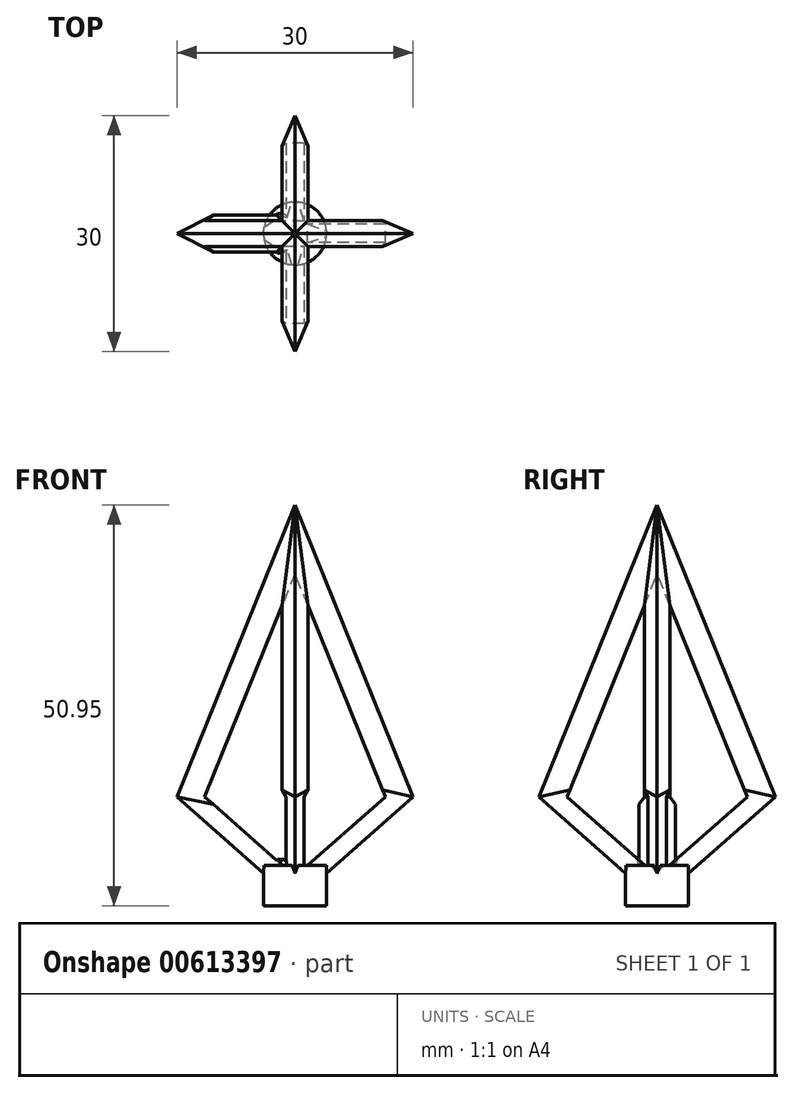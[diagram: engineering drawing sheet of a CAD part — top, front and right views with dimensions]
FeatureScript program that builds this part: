
annotation { "Feature Type Name" : "Feature", "Feature Type Description" : "" }
export const myFeature = defineFeature(function(context is Context, id is Id, definition is map)
    precondition{}
    {
        {
            var Q0;
            Q0=qCreatedBy(makeId("Front.planeOp"),FACE);
            var sketch = newSketch(context, id + "F0", { "sketchPlane" : qUnion([Q0])});
            skLineSegment(sketch, "E0", {"start": v(0, 91.96) * mm, "end": v(15, 54.88) * mm});
            skLineSegment(sketch, "E1", {"start": v(15, 54.88) * mm, "end": v(0, 41.65) * mm});
            skLineSegment(sketch, "E2", {"start": v(0, 41.65) * mm, "end": v(-15, 54.88) * mm});
            skLineSegment(sketch, "E3", {"start": v(-15, 54.88) * mm, "end": v(0, 91.96) * mm});
            skLineSegment(sketch, "E4", {"start": v(0, 41.65) * mm, "end": v(0, 91.96) * mm});
            skLineSegment(sketch, "E5", {"start": v(-15, 54.88) * mm, "end": v(15, 54.88) * mm});
            skLineSegment(sketch, "E6", {"start": v(0, 83.24) * mm, "end": v(-11.47, 54.88) * mm});
            skLineSegment(sketch, "E7", {"start": v(-11.47, 54.88) * mm, "end": v(0, 44.77) * mm});
            skLineSegment(sketch, "E8", {"start": v(0, 44.77) * mm, "end": v(11.47, 54.88) * mm});
            skLineSegment(sketch, "E9", {"start": v(11.47, 54.88) * mm, "end": v(0, 83.24) * mm});
            skSolve(sketch);
        }
        {
            var Q0;
            {var subQ0=sQuery(id+"F0.wireOp",EDGE,"E3");Q0=makeQuery(id+"F0.imprint","IMPRINT",FACE,{"disambiguationData":[TD([[makeQuery(id+"F0.imprint","IMPRINT",EDGE,{"derivedFrom":subQ0}),-1.0]])]});}
            var Q1;
            {var subQ0=sQuery(id+"F0.wireOp",EDGE,"E0");Q1=makeQuery(id+"F0.imprint","IMPRINT",FACE,{"disambiguationData":[TD([[makeQuery(id+"F0.imprint","IMPRINT",EDGE,{"derivedFrom":subQ0}),-1.0]])]});}
            var Q2;
            {var subQ0=sQuery(id+"F0.wireOp",EDGE,"E1");Q2=makeQuery(id+"F0.imprint","IMPRINT",FACE,{"disambiguationData":[TD([[makeQuery(id+"F0.imprint","IMPRINT",EDGE,{"derivedFrom":subQ0}),-1.0]])]});}
            var Q3;
            {var subQ0=sQuery(id+"F0.wireOp",EDGE,"E2");Q3=makeQuery(id+"F0.imprint","IMPRINT",FACE,{"disambiguationData":[TD([[makeQuery(id+"F0.imprint","IMPRINT",EDGE,{"derivedFrom":subQ0}),-1.0]])]});}
            extrude(context, id + "F1", {"entities" : qUnion([Q0, Q1, Q2, Q3]), "endBound" : BoundingType.SYMMETRIC, "depth" : 5 * mm, "offsetDistance" : 25 * mm});
        }
        {
            var Q0;
            Q0=qCreatedBy(makeId("Right.planeOp"),FACE);
            var sketch = newSketch(context, id + "F2", { "sketchPlane" : qUnion([Q0])});
            skLineSegment(sketch, "E10", {"start": v(0, 91.96) * mm, "end": v(15, 54.88) * mm});
            skLineSegment(sketch, "E11", {"start": v(15, 54.88) * mm, "end": v(0, 41.65) * mm});
            skLineSegment(sketch, "E12", {"start": v(0, 41.65) * mm, "end": v(-15, 54.88) * mm});
            skLineSegment(sketch, "E13", {"start": v(-15, 54.88) * mm, "end": v(0, 91.96) * mm});
            skLineSegment(sketch, "E14", {"start": v(0, 41.65) * mm, "end": v(0, 91.96) * mm});
            skLineSegment(sketch, "E15", {"start": v(-15, 54.88) * mm, "end": v(15, 54.88) * mm});
            skLineSegment(sketch, "E16", {"start": v(0, 83.24) * mm, "end": v(-11.47, 54.88) * mm});
            skLineSegment(sketch, "E17", {"start": v(-11.47, 54.88) * mm, "end": v(0, 44.77) * mm});
            skLineSegment(sketch, "E18", {"start": v(0, 44.77) * mm, "end": v(11.47, 54.88) * mm});
            skLineSegment(sketch, "E19", {"start": v(11.47, 54.88) * mm, "end": v(0, 83.24) * mm});
            skSolve(sketch);
        }
        {
            var Q0;
            {var subQ0=sQuery(id+"F2.wireOp",EDGE,"E13");Q0=makeQuery(id+"F2.imprint","IMPRINT",FACE,{"disambiguationData":[TD([[makeQuery(id+"F2.imprint","IMPRINT",EDGE,{"derivedFrom":subQ0}),-1.0]])]});}
            var Q1;
            {var subQ0=sQuery(id+"F2.wireOp",EDGE,"E12");Q1=makeQuery(id+"F2.imprint","IMPRINT",FACE,{"disambiguationData":[TD([[makeQuery(id+"F2.imprint","IMPRINT",EDGE,{"derivedFrom":subQ0}),-1.0]])]});}
            var Q2;
            {var subQ0=sQuery(id+"F2.wireOp",EDGE,"E10");Q2=makeQuery(id+"F2.imprint","IMPRINT",FACE,{"disambiguationData":[TD([[makeQuery(id+"F2.imprint","IMPRINT",EDGE,{"derivedFrom":subQ0}),-1.0]])]});}
            var Q3;
            {var subQ0=sQuery(id+"F2.wireOp",EDGE,"E11");Q3=makeQuery(id+"F2.imprint","IMPRINT",FACE,{"disambiguationData":[TD([[makeQuery(id+"F2.imprint","IMPRINT",EDGE,{"derivedFrom":subQ0}),-1.0]])]});}
            extrude(context, id + "F3", {"entities" : qUnion([Q0, Q1, Q2, Q3]), "operationType" : NewBodyOperationType.ADD, "endBound" : BoundingType.SYMMETRIC, "depth" : 5 * mm, "offsetDistance" : 25 * mm});
        }
        {
            var Q0;
            {var subQ0=sQuery(id+"F2.wireOp",EDGE,"E12");var subQ1=sQuery(id+"F2.wireOp",EDGE,"E13");Q0=makeQuery(id+"F3.boolean.opBoolean","SPLIT",EDGE,{"disambiguationData":[TD([makeQuery(id+"F3.opExtrude","SWEPT_FACE",FACE,{"disambiguationData":[OSD([subQ0])]})])],"derivedFrom":makeQuery(id+"F3.opExtrude","CAP_EDGE",EDGE,{"disambiguationData":[OSD([subQ1])],"isStart":false})});}
            chamfer(context, id + "F4", {"entities" : qUnion([Q0]), "chamferType" : ChamferType.TWO_OFFSETS, "width1" : 2.5 * mm, "oppositeDirection" : false, "width2" : 5 * mm, "tangentPropagation" : true});
        }
        {
            var Q0;
            {var subQ0=sQuery(id+"F2.wireOp",EDGE,"E12");var subQ1=sQuery(id+"F2.wireOp",EDGE,"E13");Q0=makeQuery(id+"F3.boolean.opBoolean","SPLIT",EDGE,{"disambiguationData":[TD([makeQuery(id+"F3.opExtrude","SWEPT_FACE",FACE,{"disambiguationData":[OSD([subQ0])]})])],"derivedFrom":makeQuery(id+"F3.opExtrude","CAP_EDGE",EDGE,{"disambiguationData":[OSD([subQ1])],"isStart":true})});}
            chamfer(context, id + "F5", {"entities" : qUnion([Q0]), "chamferType" : ChamferType.TWO_OFFSETS, "width1" : 5 * mm, "oppositeDirection" : false, "width2" : 2.5 * mm, "tangentPropagation" : true});
        }
        {
            var Q0;
            {var subQ0=sQuery(id+"F2.wireOp",EDGE,"E13");var subQ1=sQuery(id+"F2.wireOp",EDGE,"E12");Q0=makeQuery(id+"F3.boolean.opBoolean","SPLIT",EDGE,{"disambiguationData":[TD([makeQuery(id+"F3.opExtrude","SWEPT_FACE",FACE,{"disambiguationData":[OSD([subQ0])]})])],"derivedFrom":makeQuery(id+"F3.opExtrude","CAP_EDGE",EDGE,{"disambiguationData":[OSD([subQ1])],"isStart":false})});}
            chamfer(context, id + "F6", {"entities" : qUnion([Q0]), "chamferType" : ChamferType.TWO_OFFSETS, "width1" : 2.5 * mm, "oppositeDirection" : false, "width2" : 5 * mm, "tangentPropagation" : true});
        }
        {
            var Q0;
            {var subQ0=sQuery(id+"F2.wireOp",EDGE,"E12");var subQ1=sQuery(id+"F2.wireOp",EDGE,"E13");Q0=makeQuery(id+"F3.boolean.opBoolean","SPLIT",EDGE,{"disambiguationData":[TD([makeQuery(id+"F3.opExtrude","SWEPT_FACE",FACE,{"disambiguationData":[OSD([subQ1])]})])],"derivedFrom":makeQuery(id+"F3.opExtrude","CAP_EDGE",EDGE,{"disambiguationData":[OSD([subQ0])],"isStart":true})});}
            chamfer(context, id + "F7", {"entities" : qUnion([Q0]), "chamferType" : ChamferType.TWO_OFFSETS, "width1" : 5 * mm, "oppositeDirection" : false, "width2" : 2.5 * mm, "tangentPropagation" : true});
        }
        {
            var Q0;
            {var subQ0=sQuery(id+"F2.wireOp",EDGE,"E10");var subQ1=sQuery(id+"F2.wireOp",EDGE,"E11");Q0=makeQuery(id+"F3.boolean.opBoolean","SPLIT",EDGE,{"disambiguationData":[TD([makeQuery(id+"F3.opExtrude","SWEPT_FACE",FACE,{"disambiguationData":[OSD([subQ1])]})])],"derivedFrom":makeQuery(id+"F3.opExtrude","CAP_EDGE",EDGE,{"disambiguationData":[OSD([subQ0])],"isStart":false})});}
            chamfer(context, id + "F8", {"entities" : qUnion([Q0]), "chamferType" : ChamferType.TWO_OFFSETS, "width1" : 2.5 * mm, "oppositeDirection" : false, "width2" : 5 * mm, "tangentPropagation" : true});
        }
        {
            var Q0;
            {var subQ0=sQuery(id+"F2.wireOp",EDGE,"E10");var subQ2=sQuery(id+"F2.wireOp",EDGE,"E11");Q0=makeQuery(id+"F3.boolean.opBoolean","SPLIT",EDGE,{"disambiguationData":[TD([makeQuery(id+"F3.opExtrude","SWEPT_FACE",FACE,{"disambiguationData":[OSD([subQ2])]})])],"derivedFrom":makeQuery(id+"F3.opExtrude","CAP_EDGE",EDGE,{"disambiguationData":[OSD([subQ0])],"isStart":true})});}
            chamfer(context, id + "F9", {"entities" : qUnion([Q0]), "chamferType" : ChamferType.TWO_OFFSETS, "width1" : 5 * mm, "oppositeDirection" : false, "width2" : 2.5 * mm, "tangentPropagation" : true});
        }
        {
            var Q0;
            {var subQ0=sQuery(id+"F2.wireOp",EDGE,"E11");var subQ1=sQuery(id+"F2.wireOp",EDGE,"E10");Q0=makeQuery(id+"F3.boolean.opBoolean","SPLIT",EDGE,{"disambiguationData":[TD([makeQuery(id+"F3.opExtrude","SWEPT_FACE",FACE,{"disambiguationData":[OSD([subQ1])]})])],"derivedFrom":makeQuery(id+"F3.opExtrude","CAP_EDGE",EDGE,{"disambiguationData":[OSD([subQ0])],"isStart":true})});}
            chamfer(context, id + "F10", {"entities" : qUnion([Q0]), "chamferType" : ChamferType.TWO_OFFSETS, "width1" : 5 * mm, "oppositeDirection" : false, "width2" : 2.5 * mm, "tangentPropagation" : true});
        }
        {
            var Q0;
            {var subQ0=sQuery(id+"F2.wireOp",EDGE,"E10");var subQ2=sQuery(id+"F2.wireOp",EDGE,"E11");Q0=makeQuery(id+"F3.boolean.opBoolean","SPLIT",EDGE,{"disambiguationData":[TD([makeQuery(id+"F3.opExtrude","SWEPT_FACE",FACE,{"disambiguationData":[OSD([subQ0])]})])],"derivedFrom":makeQuery(id+"F3.opExtrude","CAP_EDGE",EDGE,{"disambiguationData":[OSD([subQ2])],"isStart":false})});}
            chamfer(context, id + "F11", {"entities" : qUnion([Q0]), "chamferType" : ChamferType.TWO_OFFSETS, "width1" : 2.5 * mm, "oppositeDirection" : false, "width2" : 5 * mm, "tangentPropagation" : true});
        }
        {
            var Q0;
            {var subQ0=sQuery(id+"F0.wireOp",EDGE,"E9");var subQ1=sQuery(id+"F0.wireOp",EDGE,"E8");var subQ2=sQuery(id+"F0.wireOp",EDGE,"E7");var subQ3=sQuery(id+"F0.wireOp",EDGE,"E6");var subQ4=sQuery(id+"F0.wireOp",EDGE,"E3");var subQ5=sQuery(id+"F0.wireOp",EDGE,"E2");var subQ6=sQuery(id+"F0.wireOp",EDGE,"E1");var subQ7=sQuery(id+"F0.wireOp",EDGE,"E0");var subQ8=makeQuery(id+"F1.opExtrude","CAP_FACE",FACE,{"disambiguationData":[OSD([subQ7,subQ6,subQ5,subQ4,subQ3,subQ2,subQ1,subQ0])],"isStart":false});var subQ9=sQuery(id+"F2.wireOp",EDGE,"E19");var subQ10=sQuery(id+"F2.wireOp",EDGE,"E18");var subQ11=sQuery(id+"F2.wireOp",EDGE,"E17");var subQ12=sQuery(id+"F2.wireOp",EDGE,"E16");var subQ13=sQuery(id+"F2.wireOp",EDGE,"E13");var subQ14=sQuery(id+"F2.wireOp",EDGE,"E12");var subQ15=sQuery(id+"F2.wireOp",EDGE,"E11");var subQ16=sQuery(id+"F2.wireOp",EDGE,"E10");var subQ17=makeQuery(id+"F3.opExtrude","CAP_FACE",FACE,{"disambiguationData":[OSD([subQ16,subQ15,subQ14,subQ13,subQ12,subQ11,subQ10,subQ9])],"isStart":true});var subQ18=makeQuery(id+"F1.opExtrude","SWEPT_FACE",FACE,{"disambiguationData":[OSD([subQ4])]});var subQ19=makeQuery(id+"F1.opExtrude","SWEPT_FACE",FACE,{"disambiguationData":[OSD([subQ7])]});var subQ20=makeQuery(id+"F3.opExtrude","CAP_FACE",FACE,{"disambiguationData":[OSD([subQ16,subQ15,subQ14,subQ13,subQ12,subQ11,subQ10,subQ9])],"isStart":false});var subQ21=makeQuery(id+"F3.opExtrude","SWEPT_FACE",FACE,{"disambiguationData":[OSD([subQ13])]});var subQ22=makeQuery(id+"F1.opExtrude","SWEPT_FACE",FACE,{"disambiguationData":[OSD([subQ6])]});var subQ23=makeQuery(id+"F3.opExtrude","SWEPT_FACE",FACE,{"disambiguationData":[OSD([subQ12])]});var subQ24=makeQuery(id+"F3.opExtrude","SWEPT_FACE",FACE,{"disambiguationData":[OSD([subQ14])]});var subQ25=makeQuery(id+"F3.opExtrude","SWEPT_FACE",FACE,{"disambiguationData":[OSD([subQ11])]});var subQ26=makeQuery(id+"F1.opExtrude","SWEPT_FACE",FACE,{"disambiguationData":[OSD([subQ5])]});Q0=makeQuery(id+"F6.opChamfer","MERGE",FACE,{"derivedFrom":[makeQuery(id+"F3.boolean.opBoolean","SPLIT",FACE,{"disambiguationData":[TD([subQ8,subQ22,subQ26,subQ17,subQ20,subQ24])],"derivedFrom":subQ8}),makeQuery(id+"F5.opChamfer","MERGE",FACE,{"derivedFrom":[makeQuery(id+"F3.boolean.opBoolean","SPLIT",FACE,{"disambiguationData":[TD([subQ8,subQ26,subQ18,makeQuery(id+"F1.opExtrude","SWEPT_FACE",FACE,{"disambiguationData":[OSD([subQ3])]}),makeQuery(id+"F1.opExtrude","SWEPT_FACE",FACE,{"disambiguationData":[OSD([subQ2])]}),subQ17,subQ24,subQ21,subQ23,subQ25])],"derivedFrom":subQ8}),makeQuery(id+"F4.opChamfer","MERGE",FACE,{"derivedFrom":[makeQuery(id+"F3.boolean.opBoolean","SPLIT",FACE,{"disambiguationData":[TD([subQ19,subQ8,subQ22,makeQuery(id+"F1.opExtrude","SWEPT_FACE",FACE,{"disambiguationData":[OSD([subQ1])]}),makeQuery(id+"F1.opExtrude","SWEPT_FACE",FACE,{"disambiguationData":[OSD([subQ0])]}),subQ20,subQ24,subQ21,subQ23,subQ25])],"derivedFrom":subQ8}),makeQuery(id+"F3.boolean.opBoolean","SPLIT",FACE,{"disambiguationData":[TD([subQ19,subQ8,subQ18,subQ17,subQ20,subQ21])],"derivedFrom":subQ8})]})]})]});}
            var sketch = newSketch(context, id + "F12", { "sketchPlane" : qUnion([Q0])});
            skLineSegment(sketch, "E20", {"start": v(-2.5, 85.78) * mm, "end": v(0, 91.96) * mm});
            skLineSegment(sketch, "E21", {"start": v(0, 91.96) * mm, "end": v(2.5, 85.78) * mm});
            skLineSegment(sketch, "E22", {"start": v(2.5, 85.78) * mm, "end": v(2.5, 91.96) * mm});
            skLineSegment(sketch, "E23", {"start": v(2.5, 91.96) * mm, "end": v(-2.5, 91.96) * mm});
            skLineSegment(sketch, "E24", {"start": v(-2.5, 91.96) * mm, "end": v(-2.5, 85.78) * mm});
            skSolve(sketch);
        }
        {
            var Q0;
            {var subQ0=sQuery(id+"F12.wireOp",EDGE,"E20");Q0=makeQuery(id+"F12.imprint","IMPRINT",FACE,{"disambiguationData":[TD([[makeQuery(id+"F12.imprint","IMPRINT",EDGE,{"derivedFrom":subQ0}),1.0]])]});}
            var Q1;
            {var subQ0=sQuery(id+"F12.wireOp",EDGE,"E21");Q1=makeQuery(id+"F12.imprint","IMPRINT",FACE,{"disambiguationData":[TD([[makeQuery(id+"F12.imprint","IMPRINT",EDGE,{"derivedFrom":subQ0}),1.0]])]});}
            extrude(context, id + "F13", {"entities" : qUnion([Q0, Q1]), "operationType" : NewBodyOperationType.REMOVE, "oppositeDirection" : true, "depth" : 25 * mm, "offsetDistance" : 25 * mm});
        }
        {
            var Q0;
            {var subQ0=sQuery(id+"F0.wireOp",EDGE,"E3");var subQ4=sQuery(id+"F0.wireOp",EDGE,"E2");var subQ5=sQuery(id+"F0.wireOp",EDGE,"E0");var subQ8=makeQuery(id+"F1.opExtrude","CAP_EDGE",EDGE,{"disambiguationData":[OSD([subQ0])],"isStart":true});Q0=makeQuery(id+"F13.boolean.opBoolean","MERGE",EDGE,{"derivedFrom":[makeQuery(id+"F3.boolean.opBoolean","SPLIT",EDGE,{"disambiguationData":[TD([makeQuery(id+"F1.opExtrude","SWEPT_FACE",FACE,{"disambiguationData":[OSD([subQ5])]})])],"derivedFrom":subQ8}),makeQuery(id+"F3.boolean.opBoolean","SPLIT",EDGE,{"disambiguationData":[TD([makeQuery(id+"F1.opExtrude","SWEPT_FACE",FACE,{"disambiguationData":[OSD([subQ4])]})])],"derivedFrom":subQ8})]});}
            chamfer(context, id + "F14", {"entities" : qUnion([Q0]), "chamferType" : ChamferType.TWO_OFFSETS, "width1" : 5 * mm, "oppositeDirection" : false, "width2" : 2.5 * mm, "tangentPropagation" : true});
        }
        {
            var Q0;
            {var subQ2=sQuery(id+"F0.wireOp",EDGE,"E3");var subQ4=sQuery(id+"F0.wireOp",EDGE,"E2");var subQ5=sQuery(id+"F0.wireOp",EDGE,"E0");var subQ8=makeQuery(id+"F1.opExtrude","CAP_EDGE",EDGE,{"disambiguationData":[OSD([subQ2])],"isStart":false});Q0=makeQuery(id+"F13.boolean.opBoolean","MERGE",EDGE,{"derivedFrom":[makeQuery(id+"F3.boolean.opBoolean","SPLIT",EDGE,{"disambiguationData":[TD([makeQuery(id+"F1.opExtrude","SWEPT_FACE",FACE,{"disambiguationData":[OSD([subQ5])]})])],"derivedFrom":subQ8}),makeQuery(id+"F3.boolean.opBoolean","SPLIT",EDGE,{"disambiguationData":[TD([makeQuery(id+"F1.opExtrude","SWEPT_FACE",FACE,{"disambiguationData":[OSD([subQ4])]})])],"derivedFrom":subQ8})]});}
            chamfer(context, id + "F15", {"entities" : qUnion([Q0]), "chamferType" : ChamferType.TWO_OFFSETS, "width1" : 2.5 * mm, "oppositeDirection" : false, "width2" : 5 * mm, "tangentPropagation" : true});
        }
        {
            var Q0;
            {var subQ2=sQuery(id+"F0.wireOp",EDGE,"E1");var subQ3=sQuery(id+"F0.wireOp",EDGE,"E3");var subQ4=sQuery(id+"F0.wireOp",EDGE,"E0");var subQ8=makeQuery(id+"F1.opExtrude","CAP_EDGE",EDGE,{"disambiguationData":[OSD([subQ4])],"isStart":false});Q0=makeQuery(id+"F13.boolean.opBoolean","MERGE",EDGE,{"derivedFrom":[makeQuery(id+"F3.boolean.opBoolean","SPLIT",EDGE,{"disambiguationData":[TD([makeQuery(id+"F1.opExtrude","SWEPT_FACE",FACE,{"disambiguationData":[OSD([subQ3])]})])],"derivedFrom":subQ8}),makeQuery(id+"F3.boolean.opBoolean","SPLIT",EDGE,{"disambiguationData":[TD([makeQuery(id+"F1.opExtrude","SWEPT_FACE",FACE,{"disambiguationData":[OSD([subQ2])]})])],"derivedFrom":subQ8})]});}
            chamfer(context, id + "F16", {"entities" : qUnion([Q0]), "chamferType" : ChamferType.TWO_OFFSETS, "width1" : 2.5 * mm, "oppositeDirection" : false, "width2" : 5 * mm, "tangentPropagation" : true});
        }
        {
            var Q0;
            {var subQ2=sQuery(id+"F0.wireOp",EDGE,"E1");var subQ3=sQuery(id+"F0.wireOp",EDGE,"E3");var subQ4=sQuery(id+"F0.wireOp",EDGE,"E0");var subQ8=makeQuery(id+"F1.opExtrude","CAP_EDGE",EDGE,{"disambiguationData":[OSD([subQ4])],"isStart":true});Q0=makeQuery(id+"F13.boolean.opBoolean","MERGE",EDGE,{"derivedFrom":[makeQuery(id+"F3.boolean.opBoolean","SPLIT",EDGE,{"disambiguationData":[TD([makeQuery(id+"F1.opExtrude","SWEPT_FACE",FACE,{"disambiguationData":[OSD([subQ3])]})])],"derivedFrom":subQ8}),makeQuery(id+"F3.boolean.opBoolean","SPLIT",EDGE,{"disambiguationData":[TD([makeQuery(id+"F1.opExtrude","SWEPT_FACE",FACE,{"disambiguationData":[OSD([subQ2])]})])],"derivedFrom":subQ8})]});}
            chamfer(context, id + "F17", {"entities" : qUnion([Q0]), "chamferType" : ChamferType.TWO_OFFSETS, "width1" : 5 * mm, "oppositeDirection" : false, "width2" : 2.5 * mm, "tangentPropagation" : true});
        }
        {
            var Q0;
            {var subQ0=sQuery(id+"F0.wireOp",EDGE,"E9");var subQ1=sQuery(id+"F0.wireOp",EDGE,"E8");var subQ2=sQuery(id+"F0.wireOp",EDGE,"E7");var subQ3=sQuery(id+"F0.wireOp",EDGE,"E6");var subQ4=sQuery(id+"F0.wireOp",EDGE,"E3");var subQ5=sQuery(id+"F0.wireOp",EDGE,"E2");var subQ6=sQuery(id+"F0.wireOp",EDGE,"E1");var subQ7=sQuery(id+"F0.wireOp",EDGE,"E0");var subQ8=makeQuery(id+"F1.opExtrude","CAP_FACE",FACE,{"disambiguationData":[OSD([subQ7,subQ6,subQ5,subQ4,subQ3,subQ2,subQ1,subQ0])],"isStart":false});var subQ9=sQuery(id+"F2.wireOp",EDGE,"E19");var subQ10=sQuery(id+"F2.wireOp",EDGE,"E18");var subQ11=sQuery(id+"F2.wireOp",EDGE,"E17");var subQ12=sQuery(id+"F2.wireOp",EDGE,"E16");var subQ13=sQuery(id+"F2.wireOp",EDGE,"E13");var subQ14=sQuery(id+"F2.wireOp",EDGE,"E12");var subQ15=sQuery(id+"F2.wireOp",EDGE,"E11");var subQ16=sQuery(id+"F2.wireOp",EDGE,"E10");var subQ17=makeQuery(id+"F3.opExtrude","CAP_FACE",FACE,{"disambiguationData":[OSD([subQ16,subQ15,subQ14,subQ13,subQ12,subQ11,subQ10,subQ9])],"isStart":true});var subQ18=makeQuery(id+"F1.opExtrude","SWEPT_FACE",FACE,{"disambiguationData":[OSD([subQ4])]});var subQ19=makeQuery(id+"F1.opExtrude","SWEPT_FACE",FACE,{"disambiguationData":[OSD([subQ7])]});var subQ20=makeQuery(id+"F3.opExtrude","CAP_FACE",FACE,{"disambiguationData":[OSD([subQ16,subQ15,subQ14,subQ13,subQ12,subQ11,subQ10,subQ9])],"isStart":false});var subQ21=makeQuery(id+"F3.opExtrude","SWEPT_FACE",FACE,{"disambiguationData":[OSD([subQ13])]});var subQ22=makeQuery(id+"F1.opExtrude","SWEPT_FACE",FACE,{"disambiguationData":[OSD([subQ6])]});var subQ23=makeQuery(id+"F3.opExtrude","SWEPT_FACE",FACE,{"disambiguationData":[OSD([subQ12])]});var subQ24=makeQuery(id+"F3.opExtrude","SWEPT_FACE",FACE,{"disambiguationData":[OSD([subQ14])]});var subQ25=makeQuery(id+"F3.opExtrude","SWEPT_FACE",FACE,{"disambiguationData":[OSD([subQ11])]});var subQ26=makeQuery(id+"F1.opExtrude","SWEPT_FACE",FACE,{"disambiguationData":[OSD([subQ5])]});Q0=makeQuery(id+"F6.opChamfer","MERGE",FACE,{"derivedFrom":[makeQuery(id+"F3.boolean.opBoolean","SPLIT",FACE,{"disambiguationData":[TD([subQ8,subQ22,subQ26,subQ17,subQ20,subQ24])],"derivedFrom":subQ8}),makeQuery(id+"F5.opChamfer","MERGE",FACE,{"derivedFrom":[makeQuery(id+"F3.boolean.opBoolean","SPLIT",FACE,{"disambiguationData":[TD([subQ8,subQ26,subQ18,makeQuery(id+"F1.opExtrude","SWEPT_FACE",FACE,{"disambiguationData":[OSD([subQ3])]}),makeQuery(id+"F1.opExtrude","SWEPT_FACE",FACE,{"disambiguationData":[OSD([subQ2])]}),subQ17,subQ24,subQ21,subQ23,subQ25])],"derivedFrom":subQ8}),makeQuery(id+"F4.opChamfer","MERGE",FACE,{"derivedFrom":[makeQuery(id+"F3.boolean.opBoolean","SPLIT",FACE,{"disambiguationData":[TD([subQ19,subQ8,subQ22,makeQuery(id+"F1.opExtrude","SWEPT_FACE",FACE,{"disambiguationData":[OSD([subQ1])]}),makeQuery(id+"F1.opExtrude","SWEPT_FACE",FACE,{"disambiguationData":[OSD([subQ0])]}),subQ20,subQ24,subQ21,subQ23,subQ25])],"derivedFrom":subQ8}),makeQuery(id+"F3.boolean.opBoolean","SPLIT",FACE,{"disambiguationData":[TD([subQ19,subQ8,subQ18,subQ17,subQ20,subQ21])],"derivedFrom":subQ8})]})]})]});}
            var sketch = newSketch(context, id + "F18", { "sketchPlane" : qUnion([Q0])});
            skLineSegment(sketch, "E25", {"start": v(2.5, 43.86) * mm, "end": v(2.5, 41.65) * mm});
            skLineSegment(sketch, "E26", {"start": v(2.5, 41.65) * mm, "end": v(-2.5, 41.65) * mm});
            skLineSegment(sketch, "E27", {"start": v(-2.5, 41.65) * mm, "end": v(-2.5, 43.86) * mm});
            skLineSegment(sketch, "E28", {"start": v(-2.5, 43.86) * mm, "end": v(0, 41.65) * mm});
            skLineSegment(sketch, "E29", {"start": v(0, 41.65) * mm, "end": v(2.5, 43.86) * mm});
            skSolve(sketch);
        }
        {
            var Q0;
            {var subQ2=sQuery(id+"F18.wireOp",EDGE,"E27");Q0=makeQuery(id+"F18.imprint","IMPRINT",FACE,{"disambiguationData":[TD([[makeQuery(id+"F18.imprint","IMPRINT",EDGE,{"derivedFrom":subQ2}),-1.0]])]});}
            var Q1;
            {var subQ0=sQuery(id+"F18.wireOp",EDGE,"E25");Q1=makeQuery(id+"F18.imprint","IMPRINT",FACE,{"disambiguationData":[TD([[makeQuery(id+"F18.imprint","IMPRINT",EDGE,{"derivedFrom":subQ0}),-1.0]])]});}
            extrude(context, id + "F19", {"entities" : qUnion([Q0, Q1]), "operationType" : NewBodyOperationType.REMOVE, "oppositeDirection" : true, "depth" : 25 * mm, "offsetDistance" : 25 * mm});
        }
        {
            var Q0;
            {var subQ2=sQuery(id+"F0.wireOp",EDGE,"E1");var subQ4=sQuery(id+"F0.wireOp",EDGE,"E2");var subQ5=sQuery(id+"F0.wireOp",EDGE,"E0");var subQ8=makeQuery(id+"F1.opExtrude","CAP_EDGE",EDGE,{"disambiguationData":[OSD([subQ2])],"isStart":false});Q0=makeQuery(id+"F19.boolean.opBoolean","MERGE",EDGE,{"derivedFrom":[makeQuery(id+"F3.boolean.opBoolean","SPLIT",EDGE,{"disambiguationData":[TD([makeQuery(id+"F1.opExtrude","SWEPT_FACE",FACE,{"disambiguationData":[OSD([subQ4])]})])],"derivedFrom":subQ8}),makeQuery(id+"F3.boolean.opBoolean","SPLIT",EDGE,{"disambiguationData":[TD([makeQuery(id+"F1.opExtrude","SWEPT_FACE",FACE,{"disambiguationData":[OSD([subQ5])]})])],"derivedFrom":subQ8})]});}
            chamfer(context, id + "F20", {"entities" : qUnion([Q0]), "chamferType" : ChamferType.TWO_OFFSETS, "width1" : 2.5 * mm, "oppositeDirection" : false, "width2" : 5 * mm, "tangentPropagation" : true});
        }
        {
            var Q0;
            {var subQ0=sQuery(id+"F0.wireOp",EDGE,"E1");var subQ4=sQuery(id+"F0.wireOp",EDGE,"E2");var subQ5=sQuery(id+"F0.wireOp",EDGE,"E0");var subQ8=makeQuery(id+"F1.opExtrude","CAP_EDGE",EDGE,{"disambiguationData":[OSD([subQ0])],"isStart":true});Q0=makeQuery(id+"F19.boolean.opBoolean","MERGE",EDGE,{"derivedFrom":[makeQuery(id+"F3.boolean.opBoolean","SPLIT",EDGE,{"disambiguationData":[TD([makeQuery(id+"F1.opExtrude","SWEPT_FACE",FACE,{"disambiguationData":[OSD([subQ4])]})])],"derivedFrom":subQ8}),makeQuery(id+"F3.boolean.opBoolean","SPLIT",EDGE,{"disambiguationData":[TD([makeQuery(id+"F1.opExtrude","SWEPT_FACE",FACE,{"disambiguationData":[OSD([subQ5])]})])],"derivedFrom":subQ8})]});}
            chamfer(context, id + "F21", {"entities" : qUnion([Q0]), "chamferType" : ChamferType.TWO_OFFSETS, "width1" : 5 * mm, "oppositeDirection" : false, "width2" : 2.5 * mm, "tangentPropagation" : true});
        }
        {
            var Q0;
            {var subQ2=sQuery(id+"F0.wireOp",EDGE,"E3");var subQ3=sQuery(id+"F0.wireOp",EDGE,"E2");var subQ5=sQuery(id+"F0.wireOp",EDGE,"E1");var subQ8=makeQuery(id+"F1.opExtrude","CAP_EDGE",EDGE,{"disambiguationData":[OSD([subQ3])],"isStart":true});Q0=makeQuery(id+"F19.boolean.opBoolean","MERGE",EDGE,{"derivedFrom":[makeQuery(id+"F3.boolean.opBoolean","SPLIT",EDGE,{"disambiguationData":[TD([makeQuery(id+"F1.opExtrude","SWEPT_FACE",FACE,{"disambiguationData":[OSD([subQ5])]})])],"derivedFrom":subQ8}),makeQuery(id+"F3.boolean.opBoolean","SPLIT",EDGE,{"disambiguationData":[TD([makeQuery(id+"F1.opExtrude","SWEPT_FACE",FACE,{"disambiguationData":[OSD([subQ2])]})])],"derivedFrom":subQ8})]});}
            chamfer(context, id + "F22", {"entities" : qUnion([Q0]), "chamferType" : ChamferType.TWO_OFFSETS, "width1" : 2.5 * mm, "oppositeDirection" : false, "width2" : 2.5 * mm, "tangentPropagation" : true});
        }
        {
            var Q0;
            {var subQ2=sQuery(id+"F0.wireOp",EDGE,"E3");var subQ3=sQuery(id+"F0.wireOp",EDGE,"E2");var subQ5=sQuery(id+"F0.wireOp",EDGE,"E1");var subQ8=makeQuery(id+"F1.opExtrude","CAP_EDGE",EDGE,{"disambiguationData":[OSD([subQ3])],"isStart":false});Q0=makeQuery(id+"F19.boolean.opBoolean","MERGE",EDGE,{"derivedFrom":[makeQuery(id+"F3.boolean.opBoolean","SPLIT",EDGE,{"disambiguationData":[TD([makeQuery(id+"F1.opExtrude","SWEPT_FACE",FACE,{"disambiguationData":[OSD([subQ5])]})])],"derivedFrom":subQ8}),makeQuery(id+"F3.boolean.opBoolean","SPLIT",EDGE,{"disambiguationData":[TD([makeQuery(id+"F1.opExtrude","SWEPT_FACE",FACE,{"disambiguationData":[OSD([subQ2])]})])],"derivedFrom":subQ8})]});}
            chamfer(context, id + "F23", {"entities" : qUnion([Q0]), "width" : 2.5 * mm, "tangentPropagation" : true});
        }
        {
            var Q0;
            Q0=qCreatedBy(makeId("Top.planeOp"),FACE);
            var sketch = newSketch(context, id + "F24", { "sketchPlane" : qUnion([Q0])});
            skCircle(sketch, "E30", {"center": v(0, 0) * mm, "radius": 4 * mm});
            skSolve(sketch);
        }
        {
            var Q0;
            Q0=makeQuery(id+"F24.imprint","IMPRINT",FACE,{"disambiguationData":[TD([[makeQuery(id+"F24.imprint","IMPRINT",EDGE,{"derivedFrom":sQuery(id+"F24.wireOp",EDGE,"E30")}),1.0]])]});
            extrude(context, id + "F25", {"entities" : qUnion([Q0]), "operationType" : NewBodyOperationType.ADD, "depth" : 46.16 * mm, "offsetDistance" : 25 * mm});
        }
        {
            var Q0;
            Q0=makeQuery(id+"F25.opExtrude","CAP_FACE",FACE,{"disambiguationData":[OSD([sQuery(id+"F24.wireOp",EDGE,"E30")])],"isStart":true});
            var sketch = newSketch(context, id + "F26", { "sketchPlane" : qUnion([Q0])});
            skCircle(sketch, "E31", {"center": v(0, 0) * mm, "radius": 4 * mm});
            skSolve(sketch);
        }
        {
            var Q0;
            Q0=makeQuery(id+"F26.imprint","IMPRINT",FACE,{"disambiguationData":[TD([[makeQuery(id+"F26.imprint","IMPRINT",EDGE,{"derivedFrom":sQuery(id+"F26.wireOp",EDGE,"E31")}),-1.0]])]});
            extrude(context, id + "F27", {"entities" : qUnion([Q0]), "operationType" : NewBodyOperationType.REMOVE, "oppositeDirection" : true, "depth" : 41 * mm, "offsetDistance" : 25 * mm});
        }
    });
